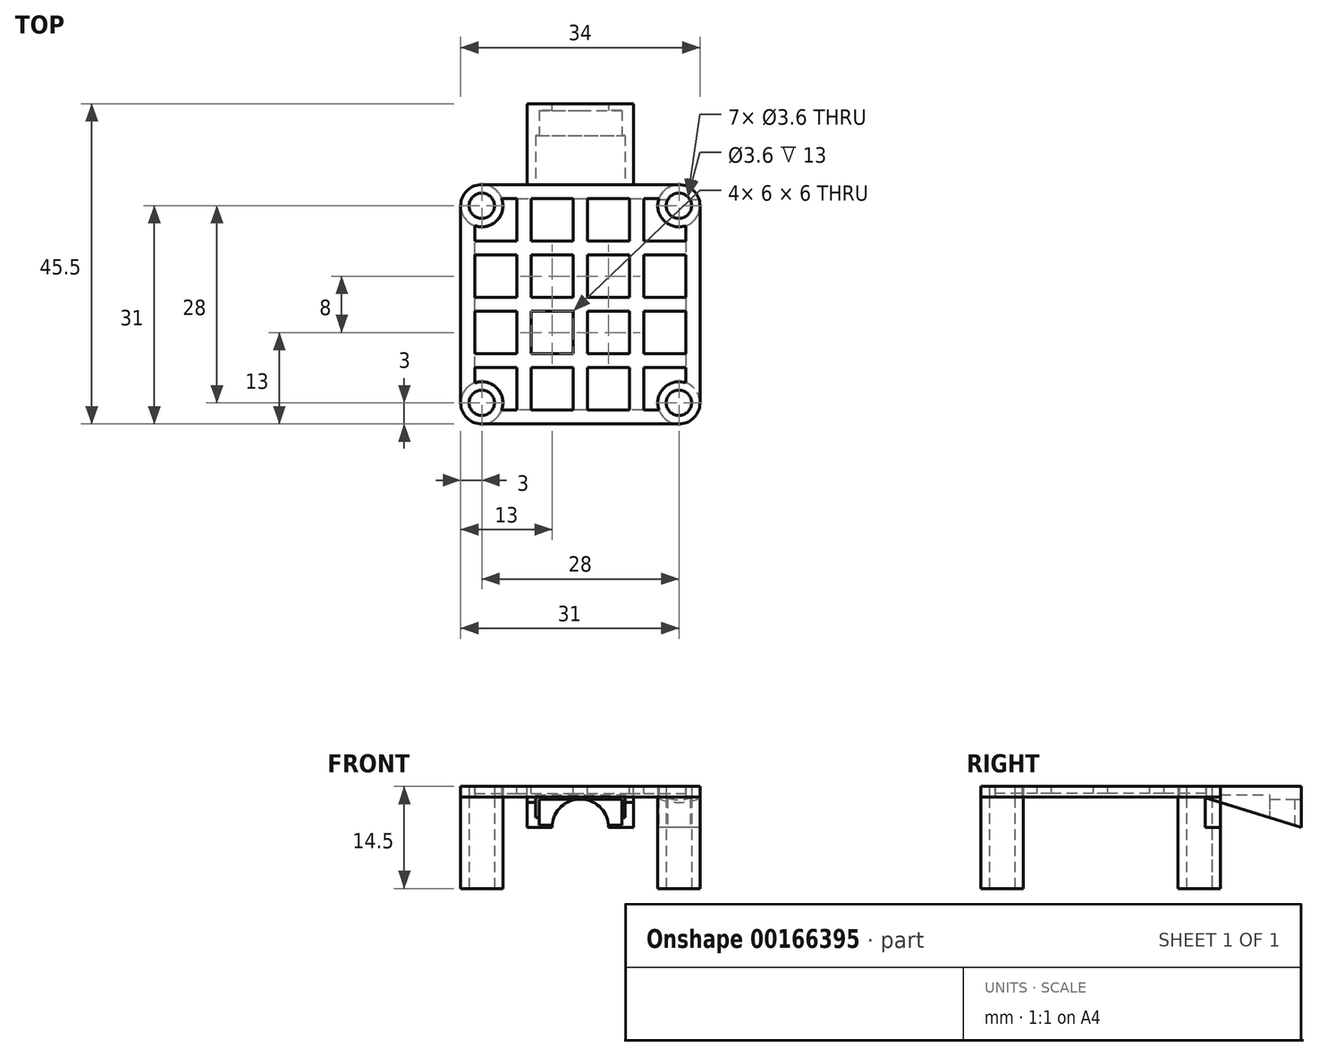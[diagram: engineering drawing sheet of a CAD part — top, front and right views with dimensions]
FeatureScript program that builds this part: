
annotation { "Feature Type Name" : "Feature", "Feature Type Description" : "" }
export const myFeature = defineFeature(function(context is Context, id is Id, definition is map)
    precondition{}
    {
        {
            var Q0;
            Q0=qCreatedBy(makeId("Top.planeOp"),FACE);
            var sketch = newSketch(context, id + "F0", { "sketchPlane" : qUnion([Q0])});
            skCircle(sketch, "E0", {"center": v(14, 14) * mm, "radius": 1.8 * mm});
            skCircle(sketch, "E1", {"center": v(-14, 14) * mm, "radius": 1.8 * mm});
            skCircle(sketch, "E2", {"center": v(-14, -14) * mm, "radius": 1.8 * mm});
            skCircle(sketch, "E3", {"center": v(14, -14) * mm, "radius": 1.8 * mm});
            skCircle(sketch, "E4", {"center": v(-14, 14) * mm, "radius": 3 * mm});
            skCircle(sketch, "E5", {"center": v(-14, -14) * mm, "radius": 3 * mm});
            skCircle(sketch, "E6", {"center": v(14, -14) * mm, "radius": 3 * mm});
            skCircle(sketch, "E7", {"center": v(14, 14) * mm, "radius": 3 * mm});
            skLineSegment(sketch, "E8", {"start": v(17, 14) * mm, "end": v(17, -14) * mm});
            skSolve(sketch);
        }
        {
            var Q0;
            Q0=qSketchRegion(id+"F0",true);
            extrude(context, id + "F1", {"entities" : qUnion([Q0]), "depth" : 13 * mm});
        }
        {
            var Q0;
            Q0=makeQuery(id+"F1.opExtrude","CAP_FACE",FACE,{"disambiguationData":[OSD([sQuery(id+"F0.wireOp",EDGE,"E0"),sQuery(id+"F0.wireOp",EDGE,"E1"),sQuery(id+"F0.wireOp",EDGE,"E2"),sQuery(id+"F0.wireOp",EDGE,"E3"),sQuery(id+"F0.wireOp",EDGE,"E4"),sQuery(id+"F0.wireOp",EDGE,"E5"),sQuery(id+"F0.wireOp",EDGE,"E6"),sQuery(id+"F0.wireOp",EDGE,"E7"),sQuery(id+"F0.wireOp",EDGE,"E8"),sQuery(id+"F0.wireOp",EDGE,"9i3S1Yhi-saMO-If9d-kcrl-0AW5lP11ECcG"),sQuery(id+"F0.wireOp",EDGE,"0W7b4J66-iXpZ-pcOm-YQU5-B3qUaQrYBzQB"),sQuery(id+"F0.wireOp",EDGE,"YHf7HNGq-JsbW-y9zw-wNTN-EviQUekIIshC")])],"isStart":false});
            var sketch = newSketch(context, id + "F2", { "sketchPlane" : qUnion([Q0])});
            skArc(sketch, "E9.0", {"start": v(-15, 11.17) * mm, "mid": v(-11.88, 11.88) * mm, "end": v(-11.17, 15) * mm});
            skCircle(sketch, "E9.1", {"center": v(-14, 14) * mm, "radius": 1.8 * mm});
            skArc(sketch, "E9.2", {"start": v(11.17, 15) * mm, "mid": v(11.88, 11.88) * mm, "end": v(15, 11.17) * mm});
            skCircle(sketch, "E9.3", {"center": v(14, 14) * mm, "radius": 1.8 * mm});
            skArc(sketch, "E9.4", {"start": v(15, -11.17) * mm, "mid": v(11.88, -11.88) * mm, "end": v(11.17, -15) * mm});
            skCircle(sketch, "E9.5", {"center": v(14, -14) * mm, "radius": 1.8 * mm});
            skCircle(sketch, "E9.6", {"center": v(-14, -14) * mm, "radius": 1.8 * mm});
            skArc(sketch, "E9.7", {"start": v(-11.17, -15) * mm, "mid": v(-11.88, -11.88) * mm, "end": v(-15, -11.17) * mm});
            skLineSegment(sketch, "E10", {"start": v(-14, 17) * mm, "end": v(14, 17) * mm});
            skLineSegment(sketch, "E11", {"start": v(17, 14) * mm, "end": v(17, -14) * mm});
            skLineSegment(sketch, "E12", {"start": v(14, -17) * mm, "end": v(-14, -17) * mm});
            skLineSegment(sketch, "E13", {"start": v(-17, -14) * mm, "end": v(-17, 14) * mm});
            skLineSegment(sketch, "E14.0", {"start": v(-15, -11.17) * mm, "end": v(-15, 11.17) * mm});
            skLineSegment(sketch, "E15.trimOffspring", {"start": v(-11.17, 15) * mm, "end": v(11.17, 15) * mm});
            skArc(sketch, "E16.trimOffspring", {"start": v(-14, 17) * mm, "mid": v(-16.12, 16.12) * mm, "end": v(-17, 14) * mm});
            skArc(sketch, "E17.trimOffspring", {"start": v(17, 14) * mm, "mid": v(16.12, 16.12) * mm, "end": v(14, 17) * mm});
            skLineSegment(sketch, "E18.trimOffspring", {"start": v(15, 11.17) * mm, "end": v(15, -11.17) * mm});
            skLineSegment(sketch, "E19.trimOffspring", {"start": v(11.17, -15) * mm, "end": v(-11.17, -15) * mm});
            skArc(sketch, "E20.trimOffspring", {"start": v(14, -17) * mm, "mid": v(16.12, -16.12) * mm, "end": v(17, -14) * mm});
            skArc(sketch, "E21.trimOffspring", {"start": v(-17, -14) * mm, "mid": v(-16.12, -16.12) * mm, "end": v(-14, -17) * mm});
            skSolve(sketch);
        }
        {
            var Q0;
            Q0=qSketchRegion(id+"F2",true);
            extrude(context, id + "F3", {"entities" : qUnion([Q0]), "depth" : 1.5 * mm});
        }
        {
            var Q0;
            Q0=makeQuery(id+"F3.opExtrude","CAP_FACE",FACE,{"disambiguationData":[OSD([sQuery(id+"F2.wireOp",EDGE,"E9.0"),sQuery(id+"F2.wireOp",EDGE,"E9.1"),sQuery(id+"F2.wireOp",EDGE,"E9.2"),sQuery(id+"F2.wireOp",EDGE,"E9.3"),sQuery(id+"F2.wireOp",EDGE,"E9.4"),sQuery(id+"F2.wireOp",EDGE,"E9.5"),sQuery(id+"F2.wireOp",EDGE,"E9.6"),sQuery(id+"F2.wireOp",EDGE,"E9.7"),sQuery(id+"F2.wireOp",EDGE,"E10"),sQuery(id+"F2.wireOp",EDGE,"E11"),sQuery(id+"F2.wireOp",EDGE,"E12"),sQuery(id+"F2.wireOp",EDGE,"E13"),sQuery(id+"F2.wireOp",EDGE,"E14.0"),sQuery(id+"F2.wireOp",EDGE,"E15.trimOffspring"),sQuery(id+"F2.wireOp",EDGE,"E16.trimOffspring"),sQuery(id+"F2.wireOp",EDGE,"E17.trimOffspring"),sQuery(id+"F2.wireOp",EDGE,"E18.trimOffspring"),sQuery(id+"F2.wireOp",EDGE,"E19.trimOffspring"),sQuery(id+"F2.wireOp",EDGE,"E20.trimOffspring"),sQuery(id+"F2.wireOp",EDGE,"E21.trimOffspring")])],"isStart":false});
            var sketch = newSketch(context, id + "F4", { "sketchPlane" : qUnion([Q0])});
            skLineSegment(sketch, "E22.0", {"start": v(-1, 15) * mm, "end": v(-1, 9) * mm});
            skLineSegment(sketch, "E23.0", {"start": v(1, 15) * mm, "end": v(1, 9) * mm});
            skLineSegment(sketch, "E24.0", {"start": v(7, 15) * mm, "end": v(7, 9) * mm});
            skLineSegment(sketch, "E25.0", {"start": v(9, 15) * mm, "end": v(9, 9) * mm});
            skLineSegment(sketch, "E26.0", {"start": v(-7, 15) * mm, "end": v(-7, 9) * mm});
            skLineSegment(sketch, "E27.0", {"start": v(-9, 15) * mm, "end": v(-9, 9) * mm});
            skLineSegment(sketch, "E28.0", {"start": v(-15, -1) * mm, "end": v(-9, -1) * mm});
            skLineSegment(sketch, "E29.0", {"start": v(-15, 1) * mm, "end": v(-9, 1) * mm});
            skLineSegment(sketch, "E30.0", {"start": v(-15, 7) * mm, "end": v(-9, 7) * mm});
            skLineSegment(sketch, "E31.0", {"start": v(-15, 9) * mm, "end": v(-9, 9) * mm});
            skLineSegment(sketch, "E32.0", {"start": v(-15, -7) * mm, "end": v(-9, -7) * mm});
            skLineSegment(sketch, "E33.0", {"start": v(-15, -9) * mm, "end": v(-9, -9) * mm});
            skLineSegment(sketch, "E34.trimOffspring", {"start": v(-7, 9) * mm, "end": v(-1, 9) * mm});
            skLineSegment(sketch, "E35.trimOffspring", {"start": v(-7, 7) * mm, "end": v(-1, 7) * mm});
            skLineSegment(sketch, "E36.trimOffspring", {"start": v(-7, 7) * mm, "end": v(-7, 1) * mm});
            skLineSegment(sketch, "E37.trimOffspring", {"start": v(-9, 7) * mm, "end": v(-9, 1) * mm});
            skLineSegment(sketch, "E38.trimOffspring", {"start": v(-1, 7) * mm, "end": v(-1, 1) * mm});
            skLineSegment(sketch, "E39.trimOffspring", {"start": v(1, 7) * mm, "end": v(1, 1) * mm});
            skLineSegment(sketch, "E40.trimOffspring", {"start": v(7, 7) * mm, "end": v(7, 1) * mm});
            skLineSegment(sketch, "E41.trimOffspring", {"start": v(9, 7) * mm, "end": v(9, 1) * mm});
            skLineSegment(sketch, "E42.trimOffspring", {"start": v(9, 9) * mm, "end": v(15, 9) * mm});
            skLineSegment(sketch, "E43.trimOffspring", {"start": v(9, 7) * mm, "end": v(15, 7) * mm});
            skLineSegment(sketch, "E44.trimOffspring", {"start": v(1, 7) * mm, "end": v(7, 7) * mm});
            skLineSegment(sketch, "E45.trimOffspring", {"start": v(1, 9) * mm, "end": v(7, 9) * mm});
            skLineSegment(sketch, "E46.trimOffspring", {"start": v(9, 1) * mm, "end": v(15, 1) * mm});
            skLineSegment(sketch, "E47.trimOffspring", {"start": v(9, -1) * mm, "end": v(15, -1) * mm});
            skLineSegment(sketch, "E48.trimOffspring", {"start": v(9, -7) * mm, "end": v(15, -7) * mm});
            skLineSegment(sketch, "E49.trimOffspring", {"start": v(9, -9) * mm, "end": v(15, -9) * mm});
            skLineSegment(sketch, "E50.trimOffspring", {"start": v(9, -9) * mm, "end": v(9, -15) * mm});
            skLineSegment(sketch, "E51.trimOffspring", {"start": v(7, -9) * mm, "end": v(7, -15) * mm});
            skLineSegment(sketch, "E52.trimOffspring", {"start": v(9, -1) * mm, "end": v(9, -7) * mm});
            skLineSegment(sketch, "E53.trimOffspring", {"start": v(7, -1) * mm, "end": v(7, -7) * mm});
            skLineSegment(sketch, "E54.trimOffspring", {"start": v(1, -9) * mm, "end": v(1, -15) * mm});
            skLineSegment(sketch, "E55.trimOffspring", {"start": v(1, -7) * mm, "end": v(7, -7) * mm});
            skLineSegment(sketch, "E56.trimOffspring", {"start": v(1, -9) * mm, "end": v(7, -9) * mm});
            skLineSegment(sketch, "E57.trimOffspring", {"start": v(-1, -9) * mm, "end": v(-1, -15) * mm});
            skLineSegment(sketch, "E58.trimOffspring", {"start": v(-7, -9) * mm, "end": v(-7, -15) * mm});
            skLineSegment(sketch, "E59.trimOffspring", {"start": v(-7, -7) * mm, "end": v(-1, -7) * mm});
            skLineSegment(sketch, "E60.trimOffspring", {"start": v(-7, -9) * mm, "end": v(-1, -9) * mm});
            skLineSegment(sketch, "E61.trimOffspring", {"start": v(-9, -9) * mm, "end": v(-9, -15) * mm});
            skLineSegment(sketch, "E62.trimOffspring", {"start": v(-7, -1) * mm, "end": v(-1, -1) * mm});
            skLineSegment(sketch, "E63.trimOffspring", {"start": v(-7, -1) * mm, "end": v(-7, -7) * mm});
            skLineSegment(sketch, "E64.trimOffspring", {"start": v(-9, -1) * mm, "end": v(-9, -7) * mm});
            skLineSegment(sketch, "E65.trimOffspring", {"start": v(-7, 1) * mm, "end": v(-1, 1) * mm});
            skLineSegment(sketch, "E66.trimOffspring", {"start": v(1, 1) * mm, "end": v(7, 1) * mm});
            skLineSegment(sketch, "E67.trimOffspring", {"start": v(1, -1) * mm, "end": v(7, -1) * mm});
            skLineSegment(sketch, "E68.trimOffspring", {"start": v(1, -1) * mm, "end": v(1, -7) * mm});
            skLineSegment(sketch, "E69.trimOffspring", {"start": v(-1, -1) * mm, "end": v(-1, -7) * mm});
            skSolve(sketch);
        }
        {
            var Q0;
            {var subQ24=sQuery(id+"F4.wireOp",EDGE,"E22.0");Q0=makeQuery(id+"F4.imprint","IMPRINT",FACE,{"disambiguationData":[TD([[makeQuery(id+"F4.imprint","IMPRINT",EDGE,{"derivedFrom":subQ24}),1.0]])]});}
            extrude(context, id + "F5", {"entities" : qUnion([Q0]), "operationType" : NewBodyOperationType.ADD, "oppositeDirection" : true, "depth" : 1 * mm});
        }
        {
            var Q0;
            {var subQ0=sQuery(id+"F2.wireOp",EDGE,"E19.trimOffspring");var subQ1=sQuery(id+"F2.wireOp",EDGE,"E18.trimOffspring");var subQ2=sQuery(id+"F2.wireOp",EDGE,"E15.trimOffspring");var subQ3=sQuery(id+"F2.wireOp",EDGE,"E14.0");Q0=makeQuery(id+"F5.boolean.opBoolean","MERGE",FACE,{"derivedFrom":[makeQuery(id+"F3.opExtrude","CAP_FACE",FACE,{"disambiguationData":[OSD([sQuery(id+"F2.wireOp",EDGE,"E9.0"),sQuery(id+"F2.wireOp",EDGE,"E9.1"),sQuery(id+"F2.wireOp",EDGE,"E9.2"),sQuery(id+"F2.wireOp",EDGE,"E9.3"),sQuery(id+"F2.wireOp",EDGE,"E9.4"),sQuery(id+"F2.wireOp",EDGE,"E9.5"),sQuery(id+"F2.wireOp",EDGE,"E9.6"),sQuery(id+"F2.wireOp",EDGE,"E9.7"),sQuery(id+"F2.wireOp",EDGE,"E10"),sQuery(id+"F2.wireOp",EDGE,"E11"),sQuery(id+"F2.wireOp",EDGE,"E12"),sQuery(id+"F2.wireOp",EDGE,"E13"),subQ3,subQ2,sQuery(id+"F2.wireOp",EDGE,"E16.trimOffspring"),sQuery(id+"F2.wireOp",EDGE,"E17.trimOffspring"),subQ1,subQ0,sQuery(id+"F2.wireOp",EDGE,"E20.trimOffspring"),sQuery(id+"F2.wireOp",EDGE,"E21.trimOffspring")])],"isStart":false}),makeQuery(id+"F5.opExtrude","CAP_FACE",FACE,{"disambiguationData":[OSD([subQ3,subQ2,subQ1,subQ0,sQuery(id+"F4.wireOp",EDGE,"E22.0"),sQuery(id+"F4.wireOp",EDGE,"E23.0"),sQuery(id+"F4.wireOp",EDGE,"E24.0"),sQuery(id+"F4.wireOp",EDGE,"E25.0"),sQuery(id+"F4.wireOp",EDGE,"E26.0"),sQuery(id+"F4.wireOp",EDGE,"E27.0"),sQuery(id+"F4.wireOp",EDGE,"E28.0"),sQuery(id+"F4.wireOp",EDGE,"E29.0"),sQuery(id+"F4.wireOp",EDGE,"E30.0"),sQuery(id+"F4.wireOp",EDGE,"E31.0"),sQuery(id+"F4.wireOp",EDGE,"E32.0"),sQuery(id+"F4.wireOp",EDGE,"E33.0"),sQuery(id+"F4.wireOp",EDGE,"E34.trimOffspring"),sQuery(id+"F4.wireOp",EDGE,"E35.trimOffspring"),sQuery(id+"F4.wireOp",EDGE,"E36.trimOffspring"),sQuery(id+"F4.wireOp",EDGE,"E37.trimOffspring"),sQuery(id+"F4.wireOp",EDGE,"E38.trimOffspring"),sQuery(id+"F4.wireOp",EDGE,"E39.trimOffspring"),sQuery(id+"F4.wireOp",EDGE,"E40.trimOffspring"),sQuery(id+"F4.wireOp",EDGE,"E41.trimOffspring"),sQuery(id+"F4.wireOp",EDGE,"E42.trimOffspring"),sQuery(id+"F4.wireOp",EDGE,"E43.trimOffspring"),sQuery(id+"F4.wireOp",EDGE,"E44.trimOffspring"),sQuery(id+"F4.wireOp",EDGE,"E45.trimOffspring"),sQuery(id+"F4.wireOp",EDGE,"E46.trimOffspring"),sQuery(id+"F4.wireOp",EDGE,"E47.trimOffspring"),sQuery(id+"F4.wireOp",EDGE,"E48.trimOffspring"),sQuery(id+"F4.wireOp",EDGE,"E49.trimOffspring"),sQuery(id+"F4.wireOp",EDGE,"E50.trimOffspring"),sQuery(id+"F4.wireOp",EDGE,"E51.trimOffspring"),sQuery(id+"F4.wireOp",EDGE,"E52.trimOffspring"),sQuery(id+"F4.wireOp",EDGE,"E53.trimOffspring"),sQuery(id+"F4.wireOp",EDGE,"E54.trimOffspring"),sQuery(id+"F4.wireOp",EDGE,"E55.trimOffspring"),sQuery(id+"F4.wireOp",EDGE,"E56.trimOffspring"),sQuery(id+"F4.wireOp",EDGE,"E57.trimOffspring"),sQuery(id+"F4.wireOp",EDGE,"E58.trimOffspring"),sQuery(id+"F4.wireOp",EDGE,"E59.trimOffspring"),sQuery(id+"F4.wireOp",EDGE,"E60.trimOffspring"),sQuery(id+"F4.wireOp",EDGE,"E61.trimOffspring"),sQuery(id+"F4.wireOp",EDGE,"E62.trimOffspring"),sQuery(id+"F4.wireOp",EDGE,"E63.trimOffspring"),sQuery(id+"F4.wireOp",EDGE,"E64.trimOffspring"),sQuery(id+"F4.wireOp",EDGE,"E65.trimOffspring"),sQuery(id+"F4.wireOp",EDGE,"E66.trimOffspring"),sQuery(id+"F4.wireOp",EDGE,"E67.trimOffspring"),sQuery(id+"F4.wireOp",EDGE,"E68.trimOffspring"),sQuery(id+"F4.wireOp",EDGE,"E69.trimOffspring")])],"isStart":true})]});}
            var sketch = newSketch(context, id + "F6", { "sketchPlane" : qUnion([Q0])});
            skLineSegment(sketch, "E70.1", {"start": v(-14, 17) * mm, "end": v(14, 17) * mm});
            skLineSegment(sketch, "E71.bottom", {"start": v(-7.57, 17) * mm, "end": v(7.58, 17) * mm});
            skLineSegment(sketch, "E71.top", {"start": v(-7.58, 28.5) * mm, "end": v(7.58, 28.5) * mm});
            skLineSegment(sketch, "E71.left", {"start": v(-7.57, 17) * mm, "end": v(-7.58, 28.5) * mm});
            skLineSegment(sketch, "E71.right", {"start": v(7.58, 17) * mm, "end": v(7.58, 28.5) * mm});
            skSolve(sketch);
        }
        {
            var Q0;
            Q0 = qSketchRegion(id + "F6", true);
            extrude(context, id + "F7", {"entities" : qUnion([Q0]), "oppositeDirection" : true, "depth" : 5.8 * mm});
        }
        {
            var Q0;
            Q0=makeQuery(id+"F7.opExtrude","CAP_FACE",FACE,{"disambiguationData":[OSD([sQuery(id+"F6.wireOp",EDGE,"E71.bottom"),sQuery(id+"F6.wireOp",EDGE,"E71.top"),sQuery(id+"F6.wireOp",EDGE,"E71.left"),sQuery(id+"F6.wireOp",EDGE,"E71.right")])],"isStart":false});
            var sketch = newSketch(context, id + "F8", { "sketchPlane" : qUnion([Q0])});
            skLineSegment(sketch, "E72.bottom", {"start": v(-6.38, -17) * mm, "end": v(6.38, -17) * mm});
            skLineSegment(sketch, "E72.top", {"start": v(-6.38, -24) * mm, "end": v(6.38, -24) * mm});
            skLineSegment(sketch, "E72.left", {"start": v(-6.38, -17) * mm, "end": v(-6.38, -24) * mm});
            skLineSegment(sketch, "E72.right", {"start": v(6.38, -17) * mm, "end": v(6.38, -24) * mm});
            skSolve(sketch);
        }
        {
            var Q0;
            Q0 = qSketchRegion(id + "F8", true);
            extrude(context, id + "F9", {"entities" : qUnion([Q0]), "operationType" : NewBodyOperationType.REMOVE, "oppositeDirection" : true, "depth" : 4.6 * mm});
        }
        {
            var Q0;
            Q0=makeQuery(id+"F7.opExtrude","CAP_FACE",FACE,{"disambiguationData":[OSD([sQuery(id+"F6.wireOp",EDGE,"E71.bottom"),sQuery(id+"F6.wireOp",EDGE,"E71.top"),sQuery(id+"F6.wireOp",EDGE,"E71.left"),sQuery(id+"F6.wireOp",EDGE,"E71.right")])],"isStart":false});
            var sketch = newSketch(context, id + "F10", { "sketchPlane" : qUnion([Q0])});
            skLineSegment(sketch, "E73.bottom", {"start": v(-5.87, -24) * mm, "end": v(5.88, -24) * mm});
            skLineSegment(sketch, "E73.top", {"start": v(-5.87, -27.56) * mm, "end": v(5.88, -27.56) * mm});
            skLineSegment(sketch, "E73.left", {"start": v(-5.87, -24) * mm, "end": v(-5.87, -27.56) * mm});
            skLineSegment(sketch, "E73.right", {"start": v(5.88, -24) * mm, "end": v(5.88, -27.56) * mm});
            skSolve(sketch);
        }
        {
            var Q0;
            Q0 = qSketchRegion(id + "F10", true);
            extrude(context, id + "F11", {"entities" : qUnion([Q0]), "operationType" : NewBodyOperationType.REMOVE, "oppositeDirection" : true, "depth" : 4 * mm});
        }
        {
            var Q0;
            Q0=makeQuery(id+"F7.opExtrude","SWEPT_FACE",FACE,{"disambiguationData":[OSD([sQuery(id+"F6.wireOp",EDGE,"E71.top")])]});
            var sketch = newSketch(context, id + "F12", { "sketchPlane" : qUnion([Q0])});
            skCircle(sketch, "E74", {"center": v(0, 8.7) * mm, "radius": 4 * mm});
            skSolve(sketch);
        }
        {
            var Q0;
            {var subQ0=sQuery(id+"F12.wireOp",EDGE,"E74");var subQ1=makeQuery(id+"F7.opExtrude","CAP_EDGE",EDGE,{"disambiguationData":[OSD([sQuery(id+"F6.wireOp",EDGE,"E71.top")])],"isStart":false});var subQ2=makeQuery(id+"F12.imprint","INTERSECT",VERTEX,{"disambiguationData":[OD(0.0)],"derivedFrom":[subQ1,subQ0]});Q0=makeQuery(id+"F12.imprint","IMPRINT",FACE,{"disambiguationData":[TD([[makeQuery(id+"F12.imprint","IMPRINT",EDGE,{"disambiguationData":[TD([[subQ2,-1.0]])],"derivedFrom":subQ0}),1.0]])]});}
            extrude(context, id + "F13", {"entities" : qUnion([Q0]), "operationType" : NewBodyOperationType.REMOVE, "endBound" : BoundingType.SYMMETRIC, "oppositeDirection" : true, "depth" : 4 * mm});
        }
        {
            var Q0;
            Q0=makeQuery(id+"F7.opExtrude","SWEPT_FACE",FACE,{"disambiguationData":[OSD([sQuery(id+"F6.wireOp",EDGE,"E71.left")])]});
            var sketch = newSketch(context, id + "F14", { "sketchPlane" : qUnion([Q0])});
            skLineSegment(sketch, "E75", {"start": v(-28.5, 8.7) * mm, "end": v(-14.84, 12.9) * mm});
            skLineSegment(sketch, "E76", {"start": v(-14.84, 12.9) * mm, "end": v(-14.84, 8.7) * mm});
            skLineSegment(sketch, "E77", {"start": v(-14.84, 8.7) * mm, "end": v(-28.5, 8.7) * mm});
            skSolve(sketch);
        }
        {
            var Q0;
            Q0 = qSketchRegion(id + "F14", true);
            extrude(context, id + "F15", {"entities" : qUnion([Q0]), "operationType" : NewBodyOperationType.REMOVE, "oppositeDirection" : true, "depth" : 25 * mm});
        }
    });
